# Revit family: Storage-Beam_Mounted-Teknion-JNBBLO-Open_Cabinet-R20161
name_source: partatom
category: Furniture
revit_build: Autodesk Revit Architecture 2016 (Build: 20150714_1515(x64)
units: mm (PartAtom-declared; Revit-internal decimal feet)

## family parameters
Always vertical = Yes
Cut with Voids When Loaded = No
OmniClass Number = 23.40.20.00
OmniClass Title = General Furniture and Specialties
Room Calculation Point = No
Shared = Yes
Work Plane-Based = No

## types (4) — shared parameters
Assembly Code = E2020200
Manufacturer = Teknion
Manufacturer Fax = 416.661.4586
Part Number = JNBBLO
Product Documentation Link = http://www.teknion.com
Product Line = Expansion Cityline
Product Page URL = http://www.teknion.com
Series = Expansion Cityline
Sustainability Data = http://www.teknion.com
URL = www.teknion.com
Unit Weight URL = http://www.teknion.com
Warranty = http://www.teknion.com

## per-type parameters (varying)
| type | Description | Fascia Finish | Magnetic Glass | Model | No Fascia |
| Magentic Glass | Beam-Mounted Cabinet - Open, Magnetic Glass, Angled, 13" Height | Back-painted Glass - K7 - Teknion - Very White | Yes | JNBBLOMA13___ | No |
| Felt Tackboard | Beam-Mounted Cabinet - Open, Felt Tackboard, Angled, 13" Height | Fabric-Teknion-RB11-Carbon | No | JNBBLOEA13___ | No |
| No Fascia | Beam-Mounted Cabinet - Open, No Fascia, Angled, 13" Height | Fabric-Teknion-RB11-Carbon | No | JNBBLONA13___ | Yes |
| Fabric Tackboard | Beam-Mounted Cabinet - Open, Fabric Tackboard, Angled, 13" Height | Fabric - Teknion - Heather Tech - R263 - Obsidian tech | No | JNBBLOFA13___ | No |

type visibility flags (boolean, named after types; folded from table):
- Magentic Glass: Yes: (none)
- Felt Tackboard: Yes: Felt Tackboard
- No Fascia: Yes: (none)
- Fabric Tackboard: Yes: Fabric Tackboard

## geometry (parser evidence)
native form markers: Sweep x2
no freeform markers — native parametric forms only
